# Revit family: Małkowski Martech_Brama_Marc-Ok EI60
name_source: partatom
category: Drzwi
units: mm (PartAtom-declared; Revit-internal decimal feet)

## family parameters
Numer OmniClass = 23.30.10.00
Oparty na płaszczyźnie roboczej = Nie
Punkt obliczania pomieszczeń = Nie
Tnij formami wycięć po wczytaniu = Nie
Tytuł OmniClass = Doors
Współdzielony = Nie
Zawsze pionowo = Nie

## types (8) — shared parameters
IfcExportAs = IfcDoor
Montaż napędu z lewej = Tak
Montaż napędu z prawej = Tak
Obraz typu = 062-700x600-px-scale-730-547.jpg
Odporność ogniowa = EI60
Producent = Małkowski - Martech S.A.
Prowadnica = wnętrze blacha stalowa ocynkowana 1,5-2,0mm, maskownica blacha 0,7mm
Płaszcz kurtyny = elastyczny, 3-warstwowy płaszcz, grubość 10mm, kolor szary
Typ budowy = Kurtyna przeciwpożarowa
URL = https://www.malkowski.pl
Wał nawojowy = rura stalowa okrągła, średnica zależna od wymiarów kurtyny
Wspornik wału = blacha stalowa ocynkowana 4,0mm
Zakończenie ściany = Wg obiektu nadrzędnego
Zespół osłon = blacha stalowa 0,7mm
zero-valued in all types: Wysokość

## per-type parameters (varying)
| type | Kaseta wału montowana do nadproża | Kaseta wału montowana do stropu | Lewa prowadnica montowana korytarzowo | Lewa prowadnica montowana naściennie | Model | Prawa prowadnica montowana korytarzowo | Prawa prowadnica montowana naściennie |
| Kaseta wału do nadproża, lewa prowadnica naściennie, prawa prowadnica naściennie | Tak | Nie | Nie | Tak | OK 60 - N - NN | Nie | Tak |
| Kaseta wału do nadproża, lewa prowadnica naściennie, prawa prowadnica korytarzowo | Tak | Nie | Nie | Tak | OK 60 - N - NK | Tak | Nie |
| Kaseta wału do nadproża, lewa prowadnica korytarzowo, prawa prowadnica korytarzowo | Tak | Nie | Tak | Nie | OK 60 - N - KK | Tak | Nie |
| Kaseta wału do nadproża, lewa prowadnica korytarzowo, prawa prowadnica naściennie | Tak | Nie | Tak | Nie | OK 60 - N - KN | Nie | Tak |
| Kaseta wału do stropu, lewa prowadnica naściennie, prawa prowadnica naściennie | Nie | Tak | Nie | Tak | OK 60 - S - NN | Nie | Tak |
| Kaseta wału do stropu, lewa prowadnica naściennie, prawa prowadnica korytarzowo | Nie | Tak | Nie | Tak | OK 60 - S - NK | Tak | Nie |
| Kaseta wału do stropu, lewa prowadnica korytarzowo, prawa prowadnica korytarzowo | Nie | Tak | Tak | Nie | OK 60 - S - KK | Tak | Nie |
| Kaseta wału do stropu, lewa prowadnica korytarzowo, prawa prowadnica naściennie | Nie | Tak | Tak | Nie | OK 60 - S - KN | Nie | Tak |
